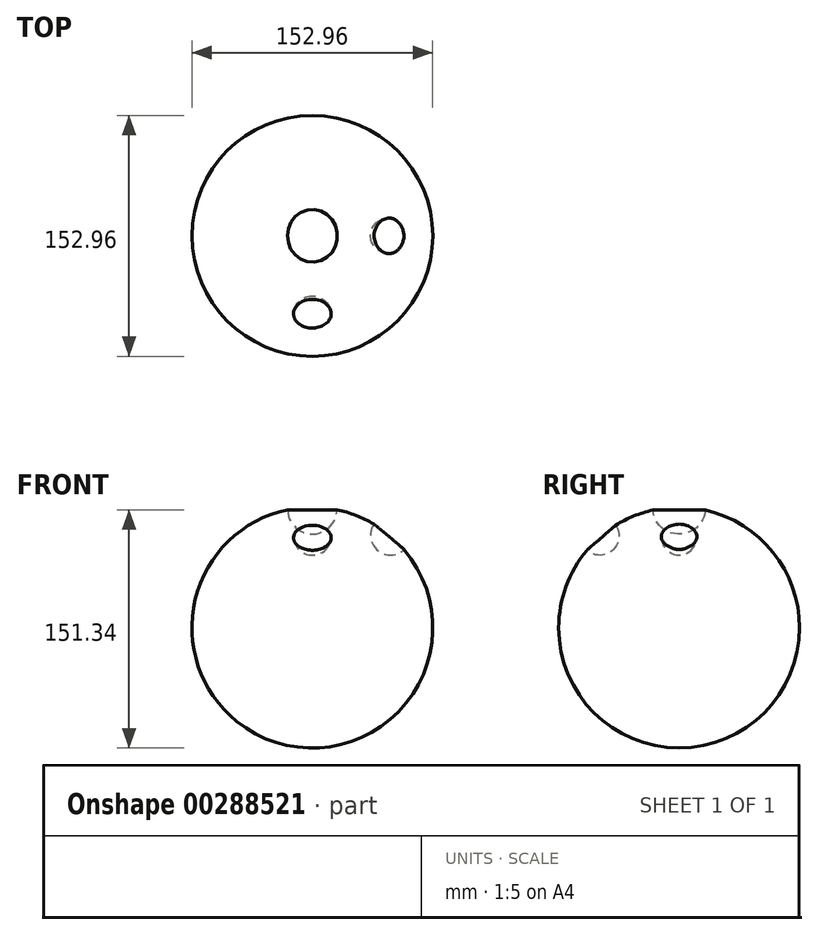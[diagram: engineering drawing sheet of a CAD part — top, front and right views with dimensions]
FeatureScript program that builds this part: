
annotation { "Feature Type Name" : "Feature", "Feature Type Description" : "" }
export const myFeature = defineFeature(function(context is Context, id is Id, definition is map)
    precondition{}
    {
        {
            var Q0;
            Q0=qCreatedBy(makeId("Top.planeOp"),FACE);
            var sketch = newSketch(context, id + "F0", { "sketchPlane" : qUnion([Q0])});
            skArc(sketch, "E0", {"start": v(0, 76.48) * mm, "mid": v(-76.48, 0) * mm, "end": v(0, -76.48) * mm});
            skLineSegment(sketch, "E1", {"start": v(0, 76.48) * mm, "end": v(0, -76.48) * mm});
            skSolve(sketch);
        }
        {
            var Q0;
            Q0=makeQuery(id+"F0.imprint","IMPRINT",FACE,{"disambiguationData":[TD([[makeQuery(id+"F0.imprint","IMPRINT",EDGE,{"derivedFrom":sQuery(id+"F0.wireOp",EDGE,"E0")}),1.0]])]});
            var Q1;
            Q1=sQuery(id+"F0.wireOp",EDGE,"E1");
            revolve(context, id + "F1", {"entities" : qUnion([Q0]), "axis" : qUnion([Q1]), "revolveType" : RevolveType.FULL});
        }
        {
            var Q0;
            Q0=qCreatedBy(makeId("Front.planeOp"),FACE);
            var sketch = newSketch(context, id + "F2", { "sketchPlane" : qUnion([Q0])});
            skArc(sketch, "E2", {"start": v(39.2, 65.93) * mm, "mid": v(41.34, 49.18) * mm, "end": v(58.23, 49.54) * mm});
            skLineSegment(sketch, "E3", {"start": v(39.2, 65.93) * mm, "end": v(58.23, 49.54) * mm});
            skSolve(sketch);
        }
        {
            var Q0;
            Q0=makeQuery(id+"F2.imprint","IMPRINT",FACE,{"disambiguationData":[TD([[makeQuery(id+"F2.imprint","IMPRINT",EDGE,{"derivedFrom":sQuery(id+"F2.wireOp",EDGE,"E2")}),1.0]])]});
            var Q1;
            Q1=sQuery(id+"F2.wireOp",EDGE,"E3");
            revolve(context, id + "F3", {"operationType" : NewBodyOperationType.REMOVE, "entities" : qUnion([Q0]), "axis" : qUnion([Q1]), "revolveType" : RevolveType.FULL, "oppositeDirection" : true});
        }
        {
            var Q0;
            Q0=qCreatedBy(makeId("Right.planeOp"),FACE);
            var sketch = newSketch(context, id + "F4", { "sketchPlane" : qUnion([Q0])});
            skArc(sketch, "E4", {"start": v(-59.68, 50.28) * mm, "mid": v(-42.62, 48.8) * mm, "end": v(-40.86, 65.83) * mm});
            skLineSegment(sketch, "E5", {"start": v(-59.68, 50.28) * mm, "end": v(-40.86, 65.83) * mm});
            skSolve(sketch);
        }
        {
            var Q0;
            Q0=makeQuery(id+"F4.imprint","IMPRINT",FACE,{"disambiguationData":[TD([[makeQuery(id+"F4.imprint","IMPRINT",EDGE,{"derivedFrom":sQuery(id+"F4.wireOp",EDGE,"E4")}),1.0]])]});
            var Q1;
            Q1=sQuery(id+"F4.wireOp",EDGE,"E5");
            revolve(context, id + "F5", {"operationType" : NewBodyOperationType.REMOVE, "entities" : qUnion([Q0]), "axis" : qUnion([Q1]), "revolveType" : RevolveType.FULL, "oppositeDirection" : true});
        }
        {
            var Q0;
            Q0=qCreatedBy(makeId("Front.planeOp"),FACE);
            var sketch = newSketch(context, id + "F6", { "sketchPlane" : qUnion([Q0])});
            skArc(sketch, "E6", {"start": v(-15.52, 77.2) * mm, "mid": v(-1.06, 59.45) * mm, "end": v(15.66, 75.08) * mm});
            skLineSegment(sketch, "E7", {"start": v(-15.52, 77.2) * mm, "end": v(15.66, 75.08) * mm});
            skSolve(sketch);
        }
        {
            var Q0;
            Q0=makeQuery(id+"F6.imprint","IMPRINT",FACE,{"disambiguationData":[TD([[makeQuery(id+"F6.imprint","IMPRINT",EDGE,{"derivedFrom":sQuery(id+"F6.wireOp",EDGE,"E6")}),1.0]])]});
            var Q1;
            Q1=sQuery(id+"F6.wireOp",EDGE,"E7");
            revolve(context, id + "F7", {"operationType" : NewBodyOperationType.REMOVE, "entities" : qUnion([Q0]), "axis" : qUnion([Q1]), "revolveType" : RevolveType.FULL, "oppositeDirection" : true});
        }
    });
